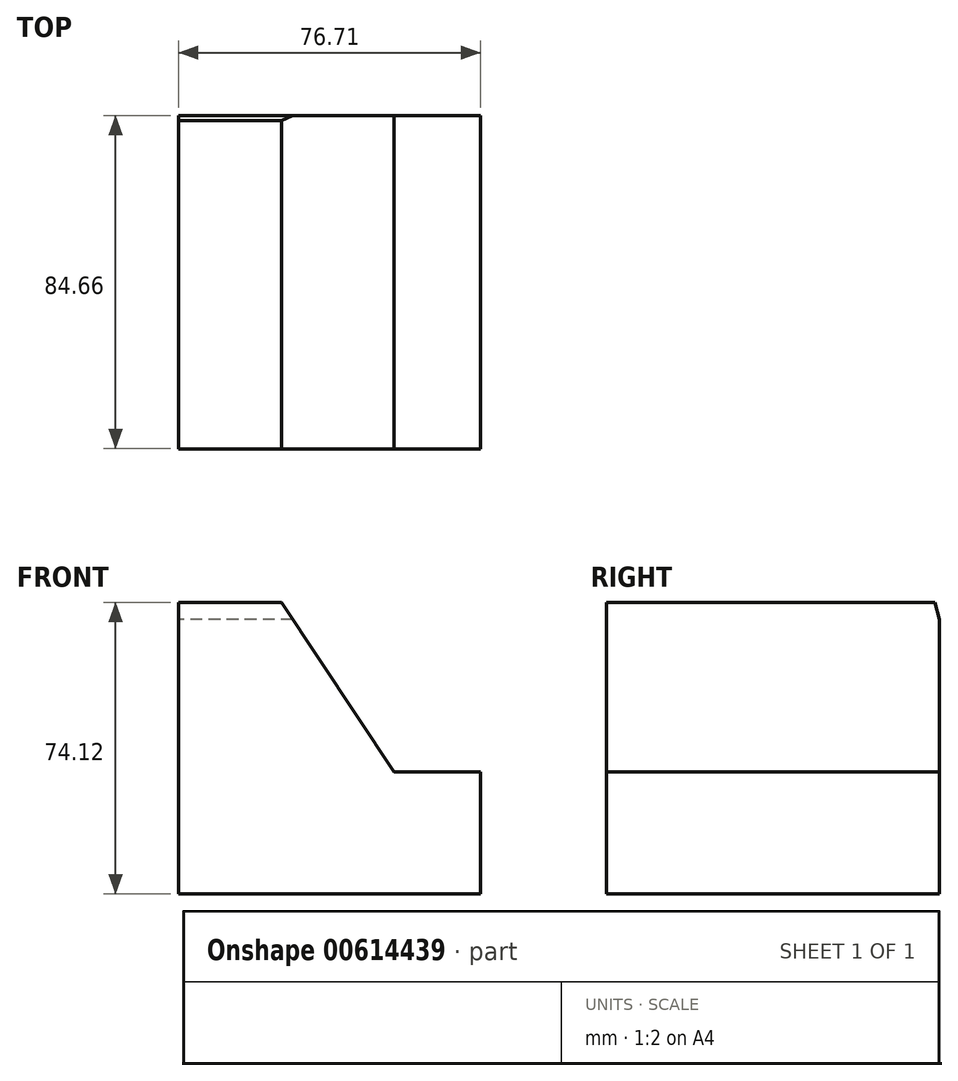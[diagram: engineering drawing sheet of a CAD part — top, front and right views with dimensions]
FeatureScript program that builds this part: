
annotation { "Feature Type Name" : "Feature", "Feature Type Description" : "" }
export const myFeature = defineFeature(function(context is Context, id is Id, definition is map)
    precondition{}
    {
        {
            var Q0;
            Q0=qCreatedBy(makeId("Right.planeOp"),FACE);
            var sketch = newSketch(context, id + "F0", { "sketchPlane" : qUnion([Q0])});
            skLineSegment(sketch, "E0", {"start": v(-51.32, 35.5) * mm, "end": v(-51.32, -38.6) * mm});
            skLineSegment(sketch, "E1", {"start": v(-51.32, -38.6) * mm, "end": v(33.34, -38.6) * mm});
            skLineSegment(sketch, "E2", {"start": v(33.34, -38.6) * mm, "end": v(33.34, 31.17) * mm});
            skLineSegment(sketch, "E3", {"start": v(-51.32, 35.5) * mm, "end": v(32.1, 35.5) * mm});
            skLineSegment(sketch, "E4", {"start": v(33.34, 31.17) * mm, "end": v(32.1, 35.5) * mm});
            skSolve(sketch);
        }
        {
            var Q0;
            Q0 = qSketchRegion(id + "F0", true);
            extrude(context, id + "F1", {"entities" : qUnion([Q0]), "depth" : 76.7 * mm, "offsetDistance" : 25.4 * mm});
        }
        {
            var Q0;
            Q0=makeQuery(id+"F1.opExtrude","SWEPT_FACE",FACE,{"disambiguationData":[OSD([sQuery(id+"F0.wireOp",EDGE,"E0")])]});
            var sketch = newSketch(context, id + "F2", { "sketchPlane" : qUnion([Q0])});
            skLineSegment(sketch, "E5", {"start": v(26.15, 35.5) * mm, "end": v(54.68, -7.6) * mm});
            skLineSegment(sketch, "E6", {"start": v(54.68, -7.6) * mm, "end": v(76.7, -7.6) * mm});
            skSolve(sketch);
        }
        {
            var Q0;
            Q0 = qSketchRegion(id + "F2", true);
            var Q1;
            {var subQ0=sQuery(id+"F2.wireOp",EDGE,"E5");Q1=makeQuery(id+"F2.imprint","IMPRINT",FACE,{"disambiguationData":[TD([[makeQuery(id+"F2.imprint","IMPRINT",EDGE,{"derivedFrom":subQ0}),1.0]])]});}
            extrude(context, id + "F3", {"entities" : qUnion([Q0, Q1]), "operationType" : NewBodyOperationType.REMOVE, "oppositeDirection" : true, "depth" : 88.4 * mm, "offsetDistance" : 25.4 * mm});
        }
    });
